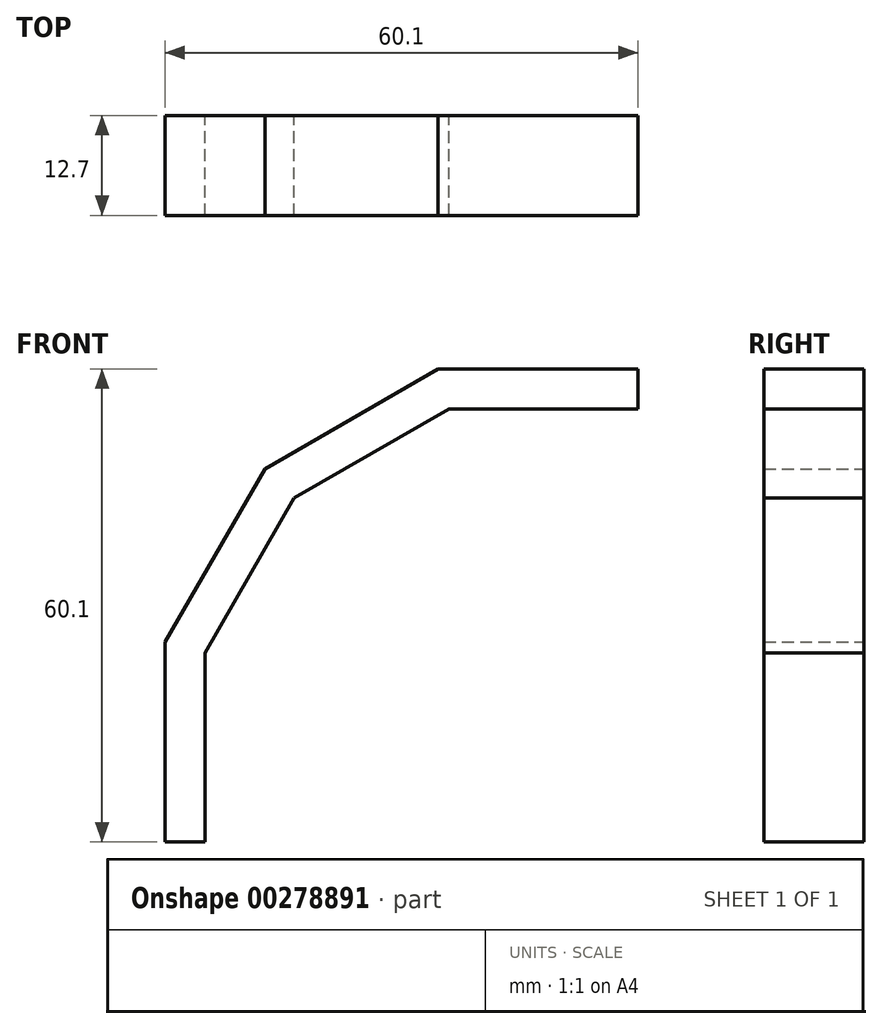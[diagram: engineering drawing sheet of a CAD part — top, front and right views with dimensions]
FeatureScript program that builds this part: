
annotation { "Feature Type Name" : "Feature", "Feature Type Description" : "" }
export const myFeature = defineFeature(function(context is Context, id is Id, definition is map)
    precondition{}
    {
        {
            var Q0;
            Q0=qCreatedBy(makeId("Front.planeOp"),FACE);
            var sketch = newSketch(context, id + "F0", { "sketchPlane" : qUnion([Q0])});
            skLineSegment(sketch, "E0", {"start": v(0, 0) * mm, "end": v(0, 25.4) * mm});
            skLineSegment(sketch, "E1", {"start": v(0, 25.4) * mm, "end": v(12.7, 47.4) * mm});
            skLineSegment(sketch, "E2", {"start": v(12.7, 47.4) * mm, "end": v(34.7, 60.1) * mm});
            skLineSegment(sketch, "E3", {"start": v(34.7, 60.1) * mm, "end": v(60.1, 60.1) * mm});
            skLineSegment(sketch, "E4.bottom", {"start": v(60.1, 60.1) * mm, "end": v(60.1, 60.1) * mm});
            skLineSegment(sketch, "E4.top", {"start": v(60.1, 55.02) * mm, "end": v(60.1, 55.02) * mm});
            skLineSegment(sketch, "E4.left", {"start": v(60.1, 60.1) * mm, "end": v(60.1, 55.02) * mm});
            skLineSegment(sketch, "E4.right", {"start": v(60.1, 60.1) * mm, "end": v(60.1, 55.02) * mm});
            skLineSegment(sketch, "E5", {"start": v(60.1, 55.02) * mm, "end": v(36.06, 55.02) * mm});
            skLineSegment(sketch, "E6", {"start": v(36.06, 55.02) * mm, "end": v(16.42, 43.68) * mm});
            skLineSegment(sketch, "E7", {"start": v(16.42, 43.68) * mm, "end": v(5.08, 24.04) * mm});
            skLineSegment(sketch, "E8", {"start": v(5.08, 24.04) * mm, "end": v(5.08, 0) * mm});
            skLineSegment(sketch, "E9", {"start": v(5.08, 0) * mm, "end": v(0, 0) * mm});
            skSolve(sketch);
        }
        {
            var Q0;
            Q0 = qSketchRegion(id + "F0", true);
            extrude(context, id + "F1", {"entities" : qUnion([Q0]), "depth" : 12.7 * mm});
        }
    });
